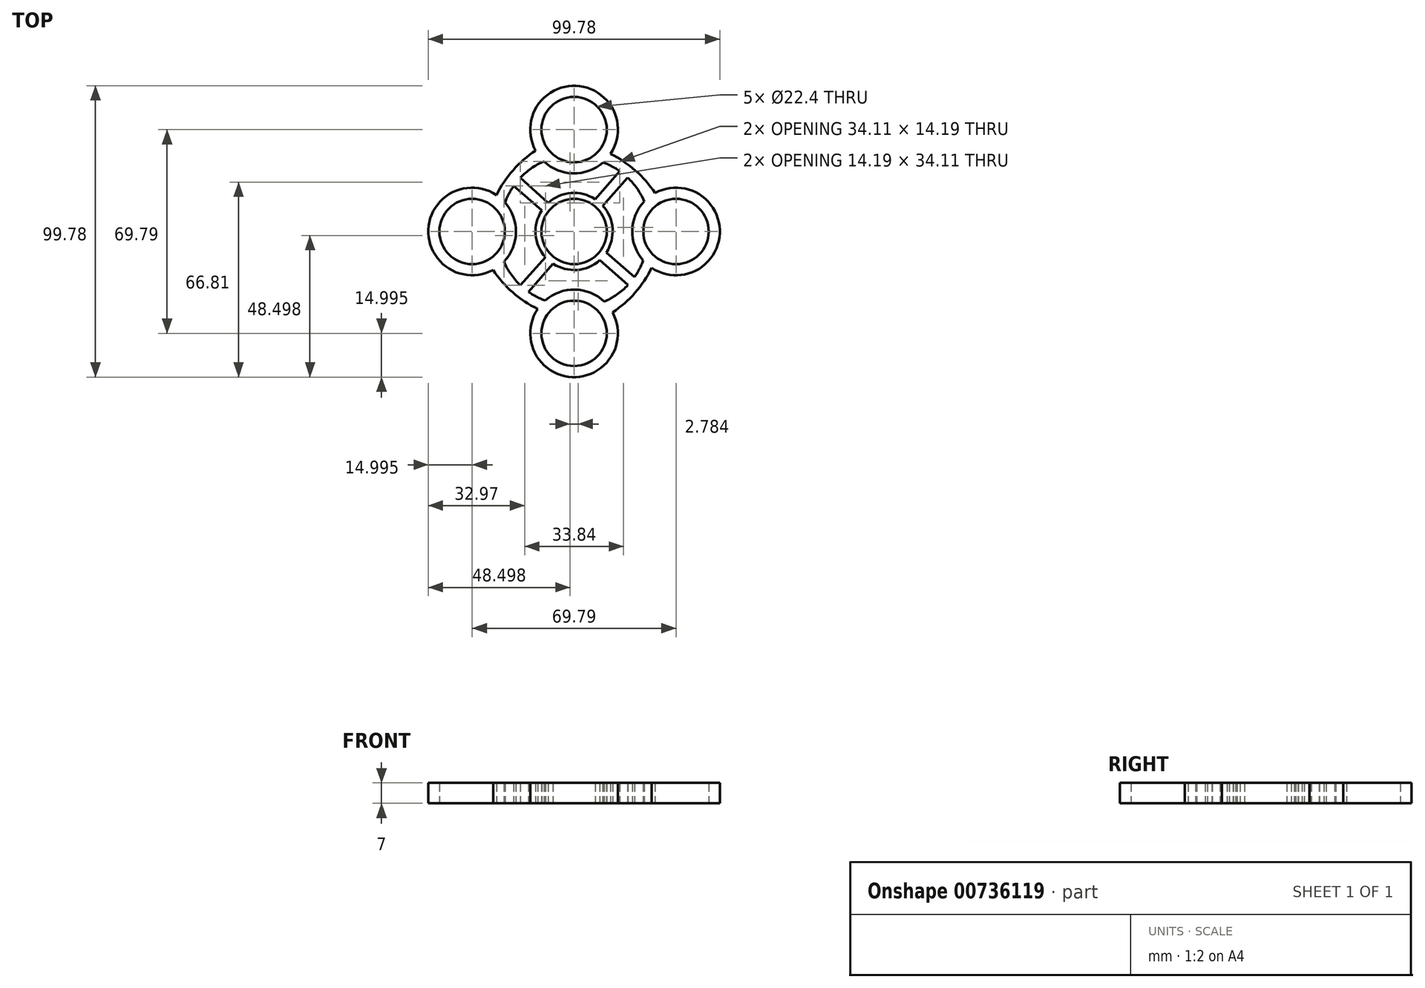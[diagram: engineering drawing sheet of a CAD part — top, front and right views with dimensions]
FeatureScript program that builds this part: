
annotation { "Feature Type Name" : "Feature", "Feature Type Description" : "" }
export const myFeature = defineFeature(function(context is Context, id is Id, definition is map)
    precondition{}
    {
        {
            var Q0;
            Q0=qCreatedBy(makeId("Top.planeOp"),FACE);
            var sketch = newSketch(context, id + "F0", { "sketchPlane" : qUnion([Q0])});
            skCircle(sketch, "E0", {"center": v(0, 0) * mm, "radius": 11.2 * mm});
            skArc(sketch, "E1", {"start": v(-11.07, 7.19) * mm, "mid": v(-13.16, -1.03) * mm, "end": v(-9.82, -8.82) * mm});
            skCircle(sketch, "E2", {"center": v(0, 34.9) * mm, "radius": 11.2 * mm});
            skArc(sketch, "E3", {"start": v(-10.33, 24.02) * mm, "mid": v(-0.27, 19.9) * mm, "end": v(9.92, 23.65) * mm});
            skArc(sketch, "E4.1.0", {"start": v(-26.57, 12.48) * mm, "mid": v(-49.88, 0.68) * mm, "end": v(-27.74, -13.18) * mm});
            skCircle(sketch, "E4.1.1", {"center": v(-34.9, 0) * mm, "radius": 11.2 * mm});
            skArc(sketch, "E4.2.0", {"start": v(10.33, -24.02) * mm, "mid": v(-11.9, -44.02) * mm, "end": v(13.18, -27.74) * mm});
            skCircle(sketch, "E4.2.1", {"center": v(0, -34.9) * mm, "radius": 11.2 * mm});
            skArc(sketch, "E4.3.0", {"start": v(26.57, -12.48) * mm, "mid": v(49.88, -0.68) * mm, "end": v(27.74, 13.18) * mm});
            skCircle(sketch, "E4.3.1", {"center": v(34.9, 0) * mm, "radius": 11.2 * mm});
            skArc(sketch, "E5", {"start": v(-13.18, 27.74) * mm, "mid": v(-20.87, 20.98) * mm, "end": v(-26.57, 12.48) * mm});
            skArc(sketch, "E6.1.0", {"start": v(-27.74, -13.18) * mm, "mid": v(-20.98, -20.87) * mm, "end": v(-12.48, -26.57) * mm});
            skArc(sketch, "E6.2.0", {"start": v(13.18, -27.74) * mm, "mid": v(20.87, -20.98) * mm, "end": v(26.57, -12.48) * mm});
            skArc(sketch, "E6.3.0", {"start": v(27.74, 13.18) * mm, "mid": v(20.98, 20.87) * mm, "end": v(12.48, 26.57) * mm});
            skArc(sketch, "E7", {"start": v(-10.33, 24.02) * mm, "mid": v(-14.68, 21.6) * mm, "end": v(-18.45, 18.35) * mm});
            skArc(sketch, "E8.1.1", {"start": v(-24.02, -10.33) * mm, "mid": v(-21.6, -14.68) * mm, "end": v(-18.35, -18.45) * mm});
            skArc(sketch, "E8.2.1", {"start": v(10.33, -24.02) * mm, "mid": v(14.68, -21.6) * mm, "end": v(18.45, -18.35) * mm});
            skArc(sketch, "E8.3.1", {"start": v(24.02, 10.33) * mm, "mid": v(21.6, 14.68) * mm, "end": v(18.35, 18.45) * mm});
            skLineSegment(sketch, "E9", {"start": v(-20.65, 15.66) * mm, "end": v(-11.07, 7.19) * mm});
            skLineSegment(sketch, "E10", {"start": v(-18.45, 18.35) * mm, "end": v(-8.82, 9.82) * mm});
            skLineSegment(sketch, "E11.1.0", {"start": v(-18.35, -18.45) * mm, "end": v(-9.82, -8.82) * mm});
            skLineSegment(sketch, "E11.1.1", {"start": v(-15.66, -20.65) * mm, "end": v(-7.19, -11.07) * mm});
            skLineSegment(sketch, "E11.2.0", {"start": v(18.45, -18.35) * mm, "end": v(8.82, -9.82) * mm});
            skLineSegment(sketch, "E11.2.1", {"start": v(20.65, -15.66) * mm, "end": v(11.07, -7.19) * mm});
            skLineSegment(sketch, "E11.3.0", {"start": v(18.35, 18.45) * mm, "end": v(9.82, 8.82) * mm});
            skLineSegment(sketch, "E11.3.1", {"start": v(15.66, 20.65) * mm, "end": v(7.19, 11.07) * mm});
            skArc(sketch, "E12.trimOffspring", {"start": v(7.19, 11.07) * mm, "mid": v(-1.03, 13.16) * mm, "end": v(-8.82, 9.82) * mm});
            skArc(sketch, "E13.trimOffspring", {"start": v(11.07, -7.19) * mm, "mid": v(13.16, 1.03) * mm, "end": v(9.82, 8.82) * mm});
            skArc(sketch, "E14.trimOffspring", {"start": v(-7.19, -11.07) * mm, "mid": v(1.03, -13.16) * mm, "end": v(8.82, -9.82) * mm});
            skArc(sketch, "E15.trimOffspring", {"start": v(15.66, 20.65) * mm, "mid": v(12.9, 22.34) * mm, "end": v(9.92, 23.65) * mm});
            skArc(sketch, "E16.trimOffspring", {"start": v(-20.65, 15.66) * mm, "mid": v(-22.34, 12.9) * mm, "end": v(-23.65, 9.92) * mm});
            skArc(sketch, "E17.trimOffspring", {"start": v(24.02, 10.33) * mm, "mid": v(19.9, 0.27) * mm, "end": v(23.65, -9.92) * mm});
            skArc(sketch, "E18.trimOffspring", {"start": v(12.48, 26.57) * mm, "mid": v(0.68, 49.88) * mm, "end": v(-13.18, 27.74) * mm});
            skArc(sketch, "E19.trimOffspring", {"start": v(-15.66, -20.65) * mm, "mid": v(-12.9, -22.34) * mm, "end": v(-9.92, -23.65) * mm});
            skArc(sketch, "E20.trimOffspring", {"start": v(20.65, -15.66) * mm, "mid": v(22.34, -12.9) * mm, "end": v(23.65, -9.92) * mm});
            skArc(sketch, "E21.trimOffspring", {"start": v(-24.02, -10.33) * mm, "mid": v(-19.9, -0.27) * mm, "end": v(-23.65, 9.92) * mm});
            skSolve(sketch);
        }
        {
            var Q0;
            Q0=makeQuery(id+"F0.imprint","IMPRINT",FACE,{"disambiguationData":[TD([[makeQuery(id+"F0.imprint","IMPRINT",EDGE,{"derivedFrom":sQuery(id+"F0.wireOp",EDGE,"E0")}),-1.0]])]});
            extrude(context, id + "F1", {"entities" : qUnion([Q0]), "depth" : 7 * mm, "offsetDistance" : 25 * mm});
        }
    });
